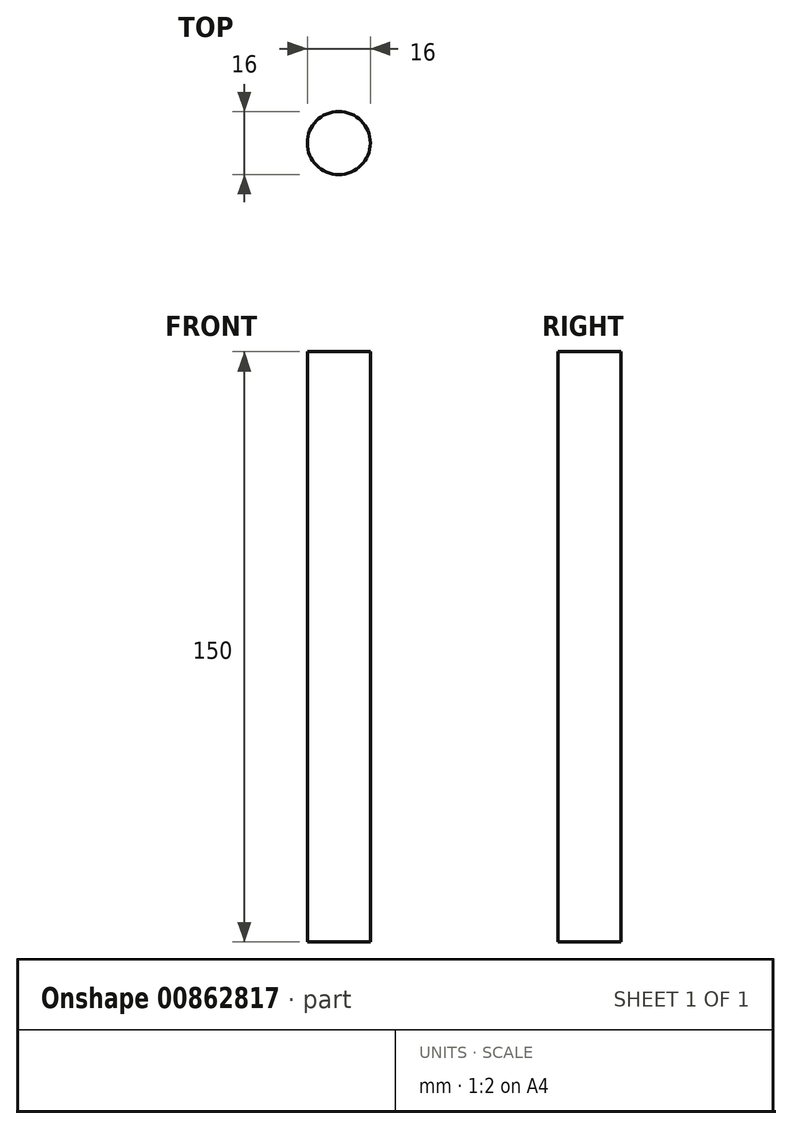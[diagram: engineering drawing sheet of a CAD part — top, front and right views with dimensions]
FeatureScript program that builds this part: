
annotation { "Feature Type Name" : "Feature", "Feature Type Description" : "" }
export const myFeature = defineFeature(function(context is Context, id is Id, definition is map)
    precondition{}
    {
        {
            var Q0;
            Q0=qCreatedBy(makeId("Top.planeOp"),FACE);
            var sketch = newSketch(context, id + "F0", { "sketchPlane" : qUnion([Q0])});
            skCircle(sketch, "E0", {"center": v(0, 0) * mm, "radius": 8 * mm});
            skSolve(sketch);
        }
        {
            var Q0;
            Q0=makeQuery(id+"F0.imprint","IMPRINT",FACE,{"disambiguationData":[TD([[makeQuery(id+"F0.imprint","IMPRINT",EDGE,{"derivedFrom":sQuery(id+"F0.wireOp",EDGE,"E0")}),1.0]])]});
            extrude(context, id + "F1", {"entities" : qUnion([Q0]), "depth" : 150 * mm, "offsetDistance" : 25 * mm});
        }
    });
